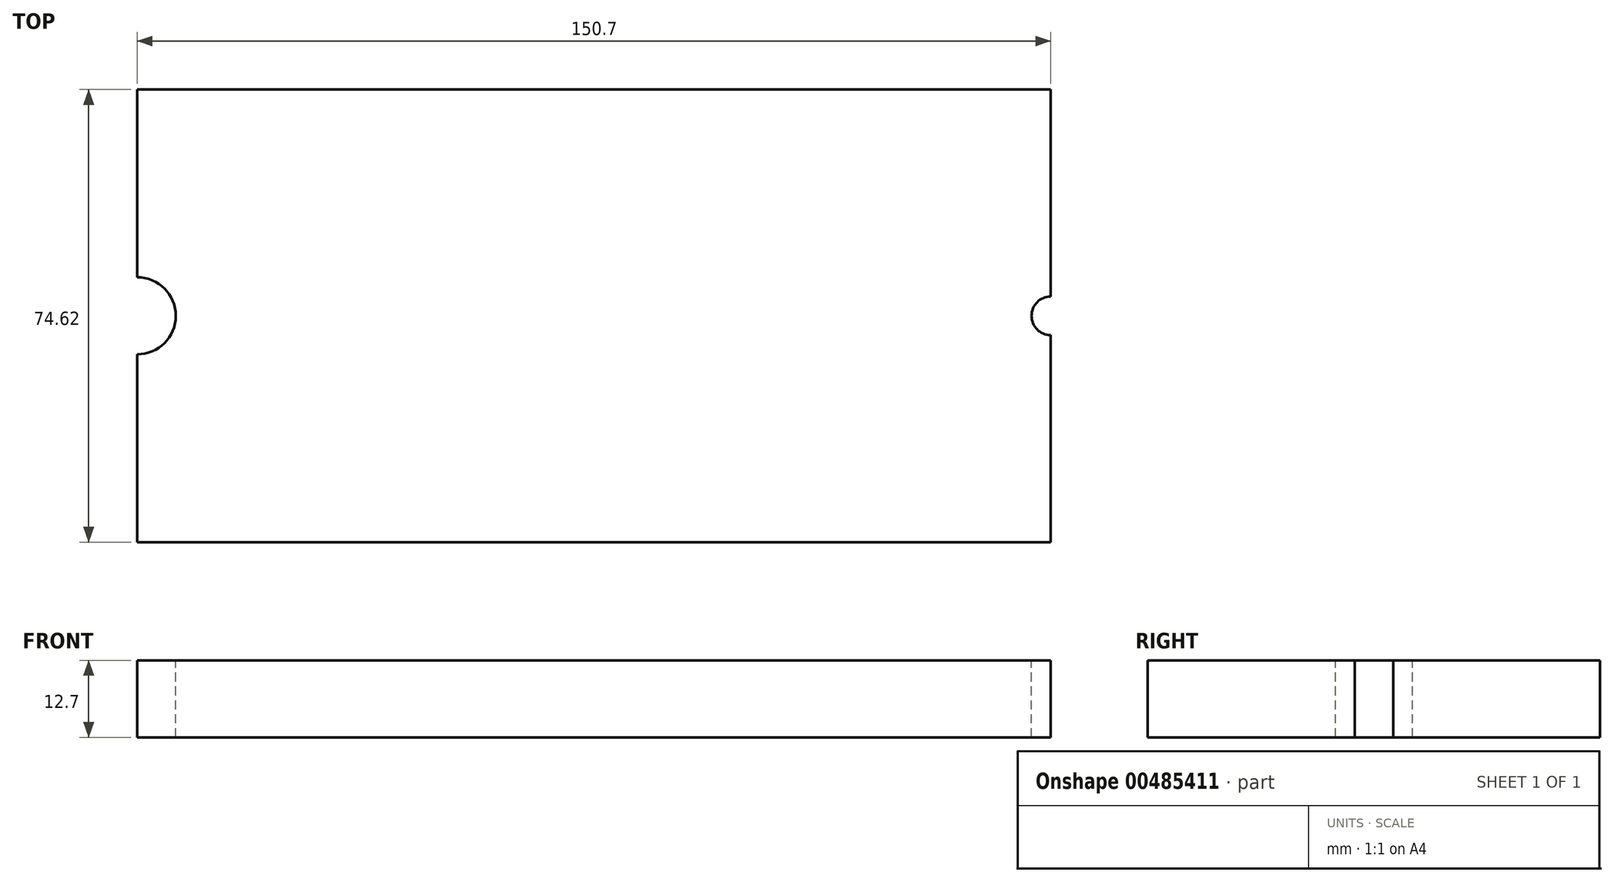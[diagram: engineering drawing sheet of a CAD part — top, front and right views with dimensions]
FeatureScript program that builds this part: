
annotation { "Feature Type Name" : "Feature", "Feature Type Description" : "" }
export const myFeature = defineFeature(function(context is Context, id is Id, definition is map)
    precondition{}
    {
        {
            var Q0;
            Q0=qCreatedBy(makeId("Top.planeOp"),FACE);
            var sketch = newSketch(context, id + "F0", { "sketchPlane" : qUnion([Q0])});
            skLineSegment(sketch, "E0.bottom", {"start": v(75.35, 37.3) * mm, "end": v(-75.35, 37.3) * mm});
            skLineSegment(sketch, "E0.top", {"start": v(75.35, -37.3) * mm, "end": v(-75.35, -37.3) * mm});
            skLineSegment(sketch, "E0.left", {"start": v(75.35, 37.3) * mm, "end": v(75.35, -37.3) * mm});
            skLineSegment(sketch, "E0.right", {"start": v(-75.35, 37.3) * mm, "end": v(-75.35, -37.3) * mm});
            skPoint(sketch, "E0.middle", {"position": v(0, 0) * mm});
            skSolve(sketch);
        }
        {
            var Q0;
            Q0 = qSketchRegion(id + "F0", true);
            extrude(context, id + "F1", {"entities" : qUnion([Q0]), "depth" : 12.7 * mm});
        }
        {
            var Q0;
            Q0=makeQuery(id+"F1.opExtrude","CAP_FACE",FACE,{"disambiguationData":[OSD([sQuery(id+"F0.wireOp",EDGE,"E0.bottom"),sQuery(id+"F0.wireOp",EDGE,"E0.top"),sQuery(id+"F0.wireOp",EDGE,"E0.left"),sQuery(id+"F0.wireOp",EDGE,"E0.right")])],"isStart":false});
            var sketch = newSketch(context, id + "F2", { "sketchPlane" : qUnion([Q0])});
            skCircle(sketch, "E1", {"center": v(75.35, 0) * mm, "radius": 5.27 * mm});
            skSolve(sketch);
        }
        {
            var Q0;
            Q0=sQuery(id+"F2.wireOp",VERTEX,"E1.center");
            var Q1;
            Q1=makeQuery(id+"F1.opExtrude","SWEPT_BODY",BODY,{"disambiguationData":[OSD([sQuery(id+"F0.wireOp",EDGE,"E0.bottom"),sQuery(id+"F0.wireOp",EDGE,"E0.top"),sQuery(id+"F0.wireOp",EDGE,"E0.left"),sQuery(id+"F0.wireOp",EDGE,"E0.right")])]});
            hole(context, id + "F3", {"style" : HoleStyle.SIMPLE, "endStyle" : HoleEndStyle.THROUGH, "holeDiameter" : 6.35 * mm, "isTappedThrough" : true, "tappedDepth" : 12.7 * mm, "tapClearance" : 3, "locations" : qUnion([Q0]), "scope" : qUnion([Q1])});
        }
        {
            var Q0;
            Q0=makeQuery(id+"F1.opExtrude","CAP_FACE",FACE,{"disambiguationData":[OSD([sQuery(id+"F0.wireOp",EDGE,"E0.bottom"),sQuery(id+"F0.wireOp",EDGE,"E0.top"),sQuery(id+"F0.wireOp",EDGE,"E0.left"),sQuery(id+"F0.wireOp",EDGE,"E0.right")])],"isStart":false});
            var sketch = newSketch(context, id + "F4", { "sketchPlane" : qUnion([Q0])});
            skCircle(sketch, "E2", {"center": v(-75.35, 0) * mm, "radius": 6.91 * mm});
            skSolve(sketch);
        }
        {
            var Q0;
            Q0=sQuery(id+"F4.wireOp",VERTEX,"E2.center");
            var Q1;
            Q1=makeQuery(id+"F1.opExtrude","SWEPT_BODY",BODY,{"disambiguationData":[OSD([sQuery(id+"F0.wireOp",EDGE,"E0.bottom"),sQuery(id+"F0.wireOp",EDGE,"E0.top"),sQuery(id+"F0.wireOp",EDGE,"E0.left"),sQuery(id+"F0.wireOp",EDGE,"E0.right")])]});
            hole(context, id + "F5", {"style" : HoleStyle.SIMPLE, "endStyle" : HoleEndStyle.THROUGH, "holeDiameter" : 12.7 * mm, "isTappedThrough" : true, "tappedDepth" : 12.7 * mm, "tapClearance" : 3, "locations" : qUnion([Q0]), "scope" : qUnion([Q1])});
        }
    });
